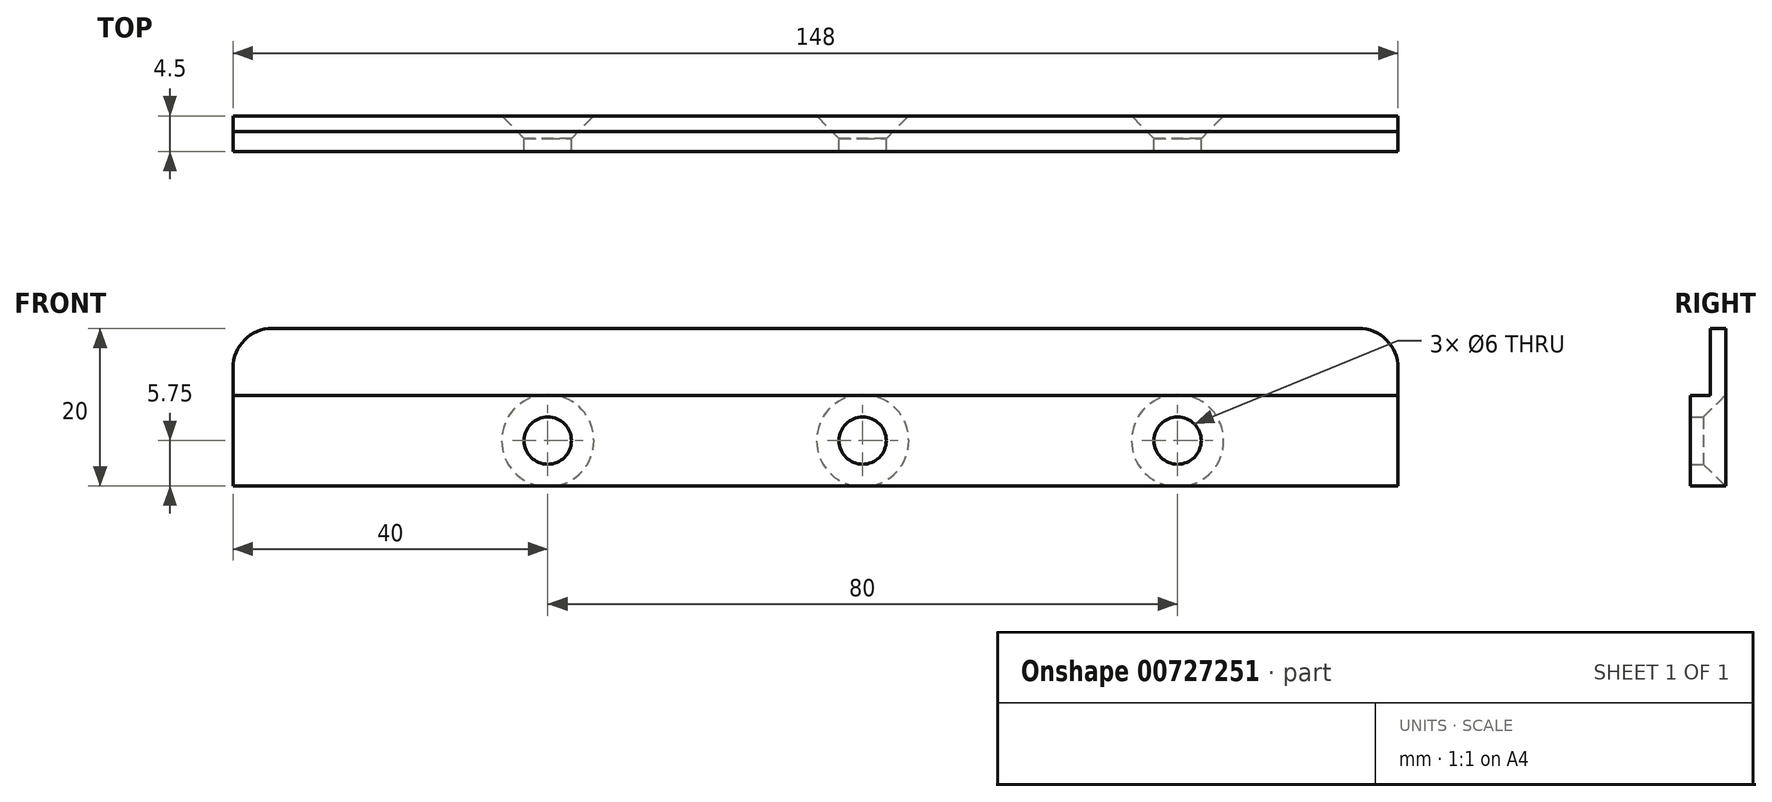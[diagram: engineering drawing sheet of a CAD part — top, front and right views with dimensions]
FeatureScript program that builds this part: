
annotation { "Feature Type Name" : "Feature", "Feature Type Description" : "" }
export const myFeature = defineFeature(function(context is Context, id is Id, definition is map)
    precondition{}
    {
        {
            var Q0;
            Q0=qCreatedBy(makeId("Front.planeOp"),FACE);
            var sketch = newSketch(context, id + "F0", { "sketchPlane" : qUnion([Q0])});
            skLineSegment(sketch, "E0.bottom", {"start": v(-74, 0) * mm, "end": v(74, 0) * mm});
            skLineSegment(sketch, "E0.top", {"start": v(-74, 11.5) * mm, "end": v(74, 11.5) * mm});
            skLineSegment(sketch, "E0.left", {"start": v(-74, 0) * mm, "end": v(-74, 11.5) * mm});
            skLineSegment(sketch, "E0.right", {"start": v(74, 0) * mm, "end": v(74, 11.5) * mm});
            skPoint(sketch, "E1", {"position": v(46, 5.75) * mm});
            skPoint(sketch, "E2.1.0.0", {"position": v(6, 5.75) * mm});
            skPoint(sketch, "E2.2.0.0", {"position": v(-34, 5.75) * mm});
            skLineSegment(sketch, "E2.direction1", {"start": v(46, 5.75) * mm, "end": v(6, 5.75) * mm, "construction": true});
            skSolve(sketch);
        }
        {
            var Q0;
            Q0 = qSketchRegion(id + "F0", true);
            extrude(context, id + "F1", {"entities" : qUnion([Q0]), "oppositeDirection" : true, "depth" : 2.5 * mm, "offsetDistance" : 25 * mm});
        }
        {
            var Q0;
            Q0=makeQuery(id+"F1.opExtrude","CAP_FACE",FACE,{"disambiguationData":[OSD([sQuery(id+"F0.wireOp",EDGE,"E0.bottom"),sQuery(id+"F0.wireOp",EDGE,"E0.top"),sQuery(id+"F0.wireOp",EDGE,"E0.left"),sQuery(id+"F0.wireOp",EDGE,"E0.right")])],"isStart":false});
            var sketch = newSketch(context, id + "F2", { "sketchPlane" : qUnion([Q0])});
            skLineSegment(sketch, "E3.bottom", {"start": v(-74, 0) * mm, "end": v(74, 0) * mm});
            skLineSegment(sketch, "E3.top", {"start": v(-74, 20) * mm, "end": v(74, 20) * mm});
            skLineSegment(sketch, "E3.left", {"start": v(-74, 0) * mm, "end": v(-74, 20) * mm});
            skLineSegment(sketch, "E3.right", {"start": v(74, 0) * mm, "end": v(74, 20) * mm});
            skSolve(sketch);
        }
        {
            var Q0;
            Q0 = qSketchRegion(id + "F2", true);
            extrude(context, id + "F3", {"entities" : qUnion([Q0]), "operationType" : NewBodyOperationType.ADD, "depth" : 2 * mm, "offsetDistance" : 25 * mm});
        }
        {
            var Q0;
            Q0=makeQuery(id+"F3.opExtrude","CAP_FACE",FACE,{"disambiguationData":[OSD([sQuery(id+"F2.wireOp",EDGE,"E3.bottom"),sQuery(id+"F2.wireOp",EDGE,"E3.top"),sQuery(id+"F2.wireOp",EDGE,"E3.left"),sQuery(id+"F2.wireOp",EDGE,"E3.right")])],"isStart":false});
            var sketch = newSketch(context, id + "F4", { "sketchPlane" : qUnion([Q0])});
            skPoint(sketch, "E4.0", {"position": v(-46, 5.75) * mm});
            skPoint(sketch, "E4.1", {"position": v(-6, 5.75) * mm});
            skPoint(sketch, "E4.2", {"position": v(34, 5.75) * mm});
            skSolve(sketch);
        }
        {
            var Q0;
            Q0=sQuery(id+"F4.wireOp",VERTEX,"E4.0");
            var Q1;
            Q1=sQuery(id+"F4.wireOp",VERTEX,"E4.1");
            var Q2;
            Q2=sQuery(id+"F4.wireOp",VERTEX,"E4.2");
            var Q3;
            Q3=makeQuery(id+"F1.opExtrude","SWEPT_BODY",BODY,{"disambiguationData":[OSD([sQuery(id+"F0.wireOp",EDGE,"E0.bottom"),sQuery(id+"F0.wireOp",EDGE,"E0.top"),sQuery(id+"F0.wireOp",EDGE,"E0.left"),sQuery(id+"F0.wireOp",EDGE,"E0.right")])]});
            hole(context, id + "F5", {"style" : HoleStyle.C_SINK, "endStyle" : HoleEndStyle.THROUGH, "holeDiameter" : 6 * mm, "cSinkDiameter" : 11.7 * mm, "cSinkAngle" : 90 * degree, "majorDiameter" : 5 * mm, "isTappedThrough" : true, "tappedDepth" : 12 * mm, "tapClearance" : 3, "locations" : qUnion([Q0, Q1, Q2]), "scope" : qUnion([Q3])});
        }
        {
            var Q0;
            Q0=makeQuery(id+"F3.opExtrude","SWEPT_EDGE",EDGE,{"disambiguationData":[OSD([sQuery(id+"F2.wireOp",EDGE,"E3.top"),sQuery(id+"F2.wireOp",EDGE,"E3.right")])]});
            var Q1;
            Q1=makeQuery(id+"F3.opExtrude","SWEPT_EDGE",EDGE,{"disambiguationData":[OSD([sQuery(id+"F2.wireOp",EDGE,"E3.top"),sQuery(id+"F2.wireOp",EDGE,"E3.left")])]});
            fillet(context, id + "F6", {"entities" : qUnion([Q0, Q1]), "radius" : 5 * mm, "tangentPropagation" : true, "allowEdgeOverflow" : false});
        }
    });
